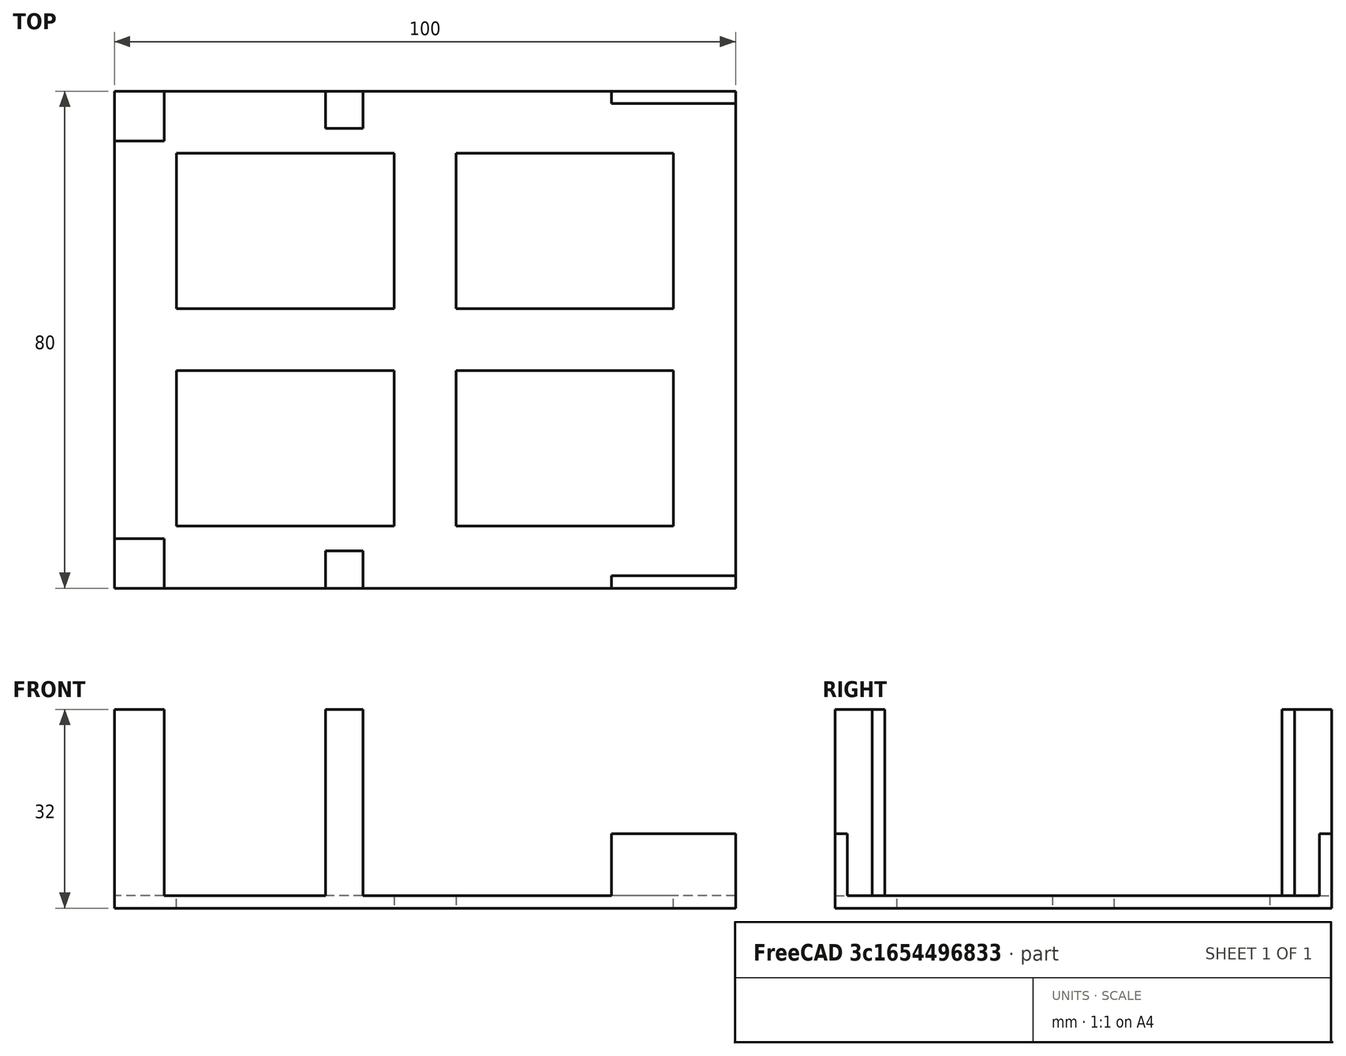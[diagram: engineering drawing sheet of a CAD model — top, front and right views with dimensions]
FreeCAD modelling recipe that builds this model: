
FCSTD DOCUMENT  (FreeCAD 0.18R16131 (Git))
Label: chassis_up
License: All rights reserved
LicenseURL: http://en.wikipedia.org/wiki/All_rights_reserved
objects: Part::Box×10, Part::MultiFuse×7, Part::Cut×2
note: 19 computed .brp shape members not serialized (recipe doc carries the construction recipe); baked Part::Feature solids carry a one-line shape summary decoded from their .brp

FEATURE [Part::Box] Box  label="Cube"
  AttacherType = Attacher::AttachEngine3D
  Height = 2
  Length = 100
  Width = 80
FEATURE [Part::Box] Box001  label="Cube001"
  AttacherType = Attacher::AttachEngine3D
  Height = 32
  Length = 8
  Width = 8
FEATURE [Part::MultiFuse] Fusion
  Shapes = -> [Box,Box001]
FEATURE [Part::Box] Box002  label="Cube002"
  AttacherType = Attacher::AttachEngine3D
  Height = 32
  Length = 8
  Placement = pos=(0,72,0) rot=(0,0,1;0rad)
  Width = 8
FEATURE [Part::MultiFuse] Fusion001
  Shapes = -> [Fusion,Box002]
FEATURE [Part::Box] Box003  label="Cube003"
  AttacherType = Attacher::AttachEngine3D
  Height = 32
  Length = 6
  Placement = pos=(34,0,0) rot=(0,0,1;0rad)
  Width = 6
FEATURE [Part::MultiFuse] Fusion002
  Shapes = -> [Fusion001,Box003]
FEATURE [Part::Box] Box004  label="Cube004"
  AttacherType = Attacher::AttachEngine3D
  Height = 32
  Length = 6
  Placement = pos=(34,74,0) rot=(0,0,1;0rad)
  Width = 6
FEATURE [Part::MultiFuse] Fusion003
  Shapes = -> [Fusion002,Box004]
FEATURE [Part::Box] Box005  label="Cube005"
  AttacherType = Attacher::AttachEngine3D
  Height = 10
  Length = 80
  Placement = pos=(10,10,0) rot=(0,0,1;0rad)
  Width = 25
FEATURE [Part::Cut] Cut
  Base = -> Fusion003
  Tool = -> Box005
FEATURE [Part::Box] Box006  label="Cube006"
  AttacherType = Attacher::AttachEngine3D
  Height = 10
  Length = 80
  Placement = pos=(10,45,0) rot=(0,0,1;0rad)
  Width = 25
FEATURE [Part::Cut] Cut001
  Base = -> Cut
  Tool = -> Box006
FEATURE [Part::Box] Box007  label="Cube007"
  AttacherType = Attacher::AttachEngine3D
  Height = 12
  Length = 20
  Placement = pos=(80,0,0) rot=(0,0,1;0rad)
  Width = 2
FEATURE [Part::MultiFuse] Fusion004
  Shapes = -> [Cut001,Box007]
FEATURE [Part::Box] Box008  label="Cube008"
  AttacherType = Attacher::AttachEngine3D
  Height = 12
  Length = 20
  Placement = pos=(80,78,0) rot=(0,0,1;0rad)
  Width = 2
FEATURE [Part::MultiFuse] Fusion005
  Shapes = -> [Fusion004,Box008]
FEATURE [Part::Box] Box009  label="Cube009"
  AttacherType = Attacher::AttachEngine3D
  Height = 2
  Length = 10
  Placement = pos=(45,0,0) rot=(0,0,1;0rad)
  Width = 80
FEATURE [Part::MultiFuse] Fusion006
  Shapes = -> [Fusion005,Box009]
